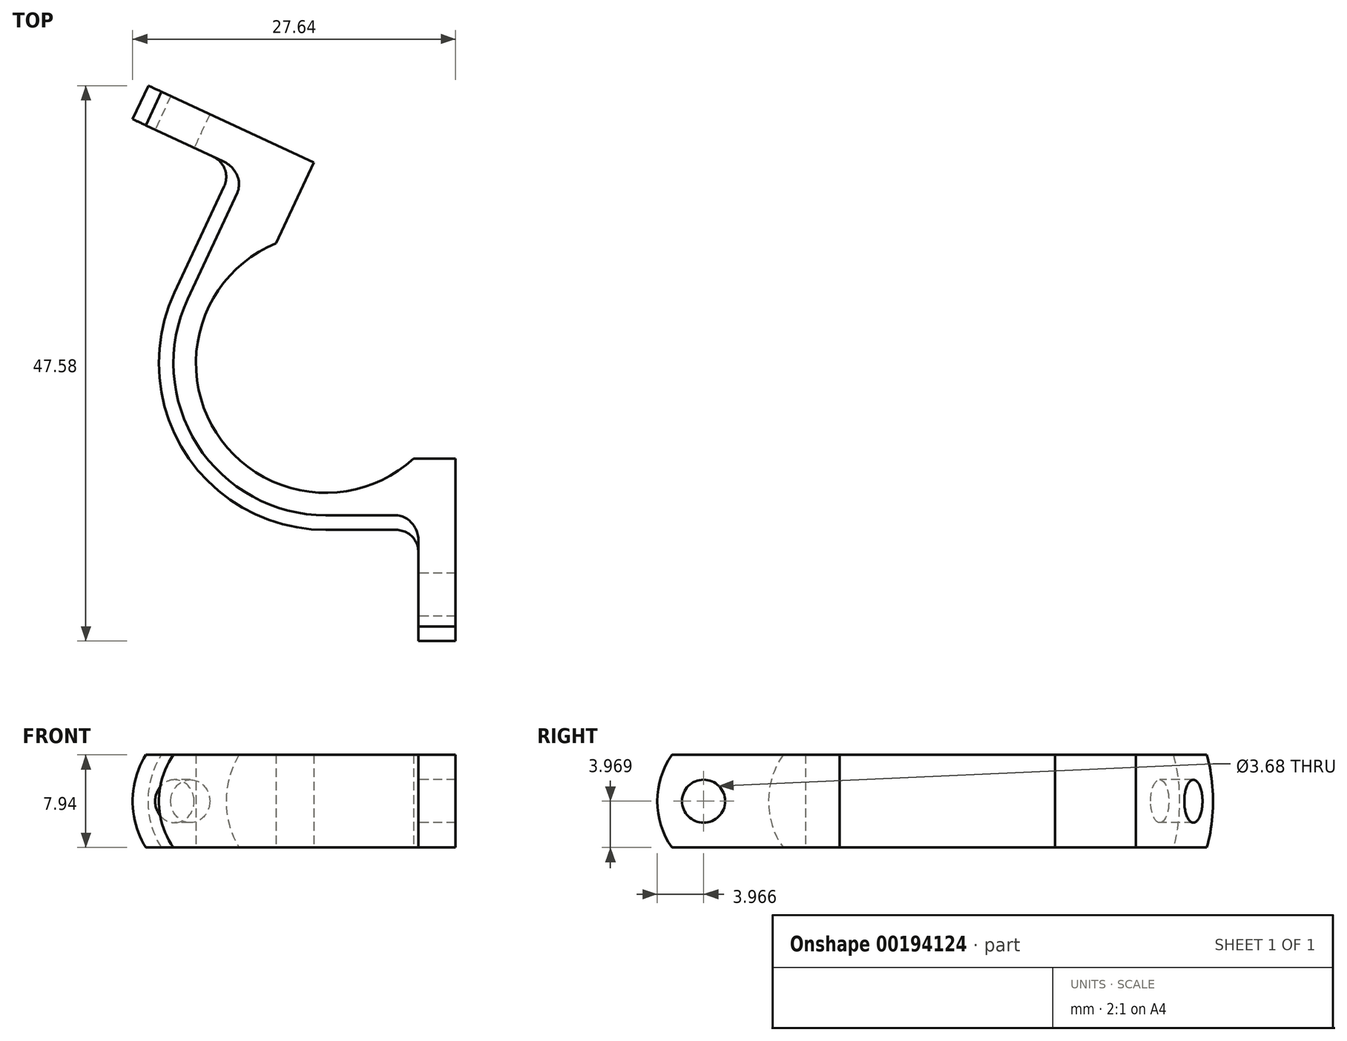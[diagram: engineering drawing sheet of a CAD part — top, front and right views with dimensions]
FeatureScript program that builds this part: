
annotation { "Feature Type Name" : "Feature", "Feature Type Description" : "" }
export const myFeature = defineFeature(function(context is Context, id is Id, definition is map)
    precondition{}
    {
        {
            var Q0;
            Q0=qCreatedBy(makeId("Top.planeOp"),FACE);
            var sketch = newSketch(context, id + "F0", { "sketchPlane" : qUnion([Q0])});
            skCircle(sketch, "E0", {"center": v(0, 0) * mm, "radius": 11.11 * mm, "construction": true});
            skLineSegment(sketch, "E1", {"start": v(11.11, -44.88) * mm, "end": v(11.11, 11.5) * mm, "construction": true});
            skLineSegment(sketch, "E2", {"start": v(11.11, 11.5) * mm, "end": v(-38.46, 34.63) * mm, "construction": true});
            skLineSegment(sketch, "E3", {"start": v(0, -11.11) * mm, "end": v(11.11, -11.11) * mm, "construction": true});
            skLineSegment(sketch, "E4", {"start": v(-10.07, 4.7) * mm, "end": v(-3.68, 18.4) * mm, "construction": true});
            skSolve(sketch);
        }
        {
            var Q0;
            Q0=qCreatedBy(makeId("Right.planeOp"),FACE);
            var sketch = newSketch(context, id + "F1", { "sketchPlane" : qUnion([Q0])});
            skLineSegment(sketch, "E5", {"start": v(-11.11, 0) * mm, "end": v(-11.11, 7.94) * mm});
            skLineSegment(sketch, "E6", {"start": v(-11.11, 7.94) * mm, "end": v(-13.04, 7.94) * mm});
            skLineSegment(sketch, "E7", {"start": v(-13.04, 0) * mm, "end": v(-11.11, 0) * mm});
            skArc(sketch, "E8", {"start": v(-13.04, 7.94) * mm, "mid": v(-14.29, 3.97) * mm, "end": v(-13.04, 0) * mm});
            skLineSegment(sketch, "E9", {"start": v(-13.04, 0) * mm, "end": v(-15.82, 3.97) * mm, "construction": true});
            skLineSegment(sketch, "E10", {"start": v(-14.29, 3.97) * mm, "end": v(-11.11, 3.97) * mm, "construction": true});
            skLineSegment(sketch, "E11", {"start": v(0, 0) * mm, "end": v(0, 7.94) * mm, "construction": true});
            skSolve(sketch);
        }
        {
            var Q0;
            Q0=makeQuery(id+"F1.imprint","IMPRINT",FACE,{"disambiguationData":[TD([[makeQuery(id+"F1.imprint","IMPRINT",EDGE,{"derivedFrom":sQuery(id+"F1.wireOp",EDGE,"E5")}),1.0]])]});
            var Q1;
            Q1=sQuery(id+"F1.wireOp",EDGE,"E11");
            revolve(context, id + "F2", {"entities" : qUnion([Q0]), "axis" : qUnion([Q1]), "revolveType" : RevolveType.FULL});
        }
        {
            var Q0;
            Q0=makeQuery(id+"F2.opRevolve","SWEPT_FACE",FACE,{"disambiguationData":[OSD([sQuery(id+"F1.wireOp",EDGE,"E6")])]});
            var sketch = newSketch(context, id + "F3", { "sketchPlane" : qUnion([Q0])});
            skArc(sketch, "E12", {"start": v(0, -11.11) * mm, "mid": v(9.37, 5.97) * mm, "end": v(-10.07, 4.7) * mm});
            skArc(sketch, "E13", {"start": v(0, -14.29) * mm, "mid": v(12.05, 7.68) * mm, "end": v(-12.95, 6.04) * mm});
            skLineSegment(sketch, "E14", {"start": v(0, 0) * mm, "end": v(-10.07, 4.7) * mm, "construction": true});
            skLineSegment(sketch, "E15", {"start": v(-10.07, 4.7) * mm, "end": v(-12.95, 6.04) * mm});
            skLineSegment(sketch, "E16", {"start": v(0, -11.11) * mm, "end": v(0, -14.29) * mm});
            skSolve(sketch);
        }
        {
            var Q0;
            Q0 = qSketchRegion(id + "F3", true);
            var Q1;
            Q1=makeQuery(id+"F2.opRevolve","SWEPT_FACE",FACE,{"disambiguationData":[OSD([sQuery(id+"F1.wireOp",EDGE,"E7")])]});
            extrude(context, id + "F4", {"entities" : qUnion([Q0]), "operationType" : NewBodyOperationType.REMOVE, "endBound" : BoundingType.UP_TO_SURFACE, "oppositeDirection" : true, "endBoundEntityFace" : qUnion([Q1]), "depth" : 25.4 * mm});
        }
        {
            var Q0;
            Q0=makeQuery(id+"F4.boolean.opBoolean","COPY",FACE,{"derivedFrom":makeQuery(id+"F4.opExtrude","SWEPT_FACE",FACE,{"disambiguationData":[OSD([sQuery(id+"F3.wireOp",EDGE,"E16")])]})});
            var Q1;
            Q1=sQuery(id+"F0.wireOp",VERTEX,"E3.end");
            extrude(context, id + "F5", {"entities" : qUnion([Q0]), "operationType" : NewBodyOperationType.ADD, "endBound" : BoundingType.UP_TO_VERTEX, "endBoundEntityVertex" : qUnion([Q1]), "depth" : 25.4 * mm});
        }
        {
            var Q0;
            Q0=makeQuery(id+"F4.boolean.opBoolean","COPY",FACE,{"derivedFrom":makeQuery(id+"F4.opExtrude","SWEPT_FACE",FACE,{"disambiguationData":[OSD([sQuery(id+"F3.wireOp",EDGE,"E15")])]})});
            var Q1;
            Q1=sQuery(id+"F0.wireOp",VERTEX,"E4.end");
            extrude(context, id + "F6", {"entities" : qUnion([Q0]), "operationType" : NewBodyOperationType.ADD, "endBound" : BoundingType.UP_TO_VERTEX, "endBoundEntityVertex" : qUnion([Q1]), "depth" : 25.4 * mm});
        }
        {
            var Q0;
            Q0=qCreatedBy(makeId("Top.planeOp"),FACE);
            var sketch = newSketch(context, id + "F7", { "sketchPlane" : qUnion([Q0])});
            skLineSegment(sketch, "E17", {"start": v(-10.07, 4.7) * mm, "end": v(0, -11.11) * mm, "construction": true});
            skLineSegment(sketch, "E18", {"start": v(0, 0) * mm, "end": v(-5.97, 9.37) * mm, "construction": true});
            skLineSegment(sketch, "E19", {"start": v(0, 0) * mm, "end": v(5.97, -9.37) * mm, "construction": true});
            skLineSegment(sketch, "E20", {"start": v(7.5, -8.2) * mm, "end": v(0, 0) * mm, "construction": true});
            skLineSegment(sketch, "E21", {"start": v(0, 0) * mm, "end": v(-4.25, 10.27) * mm, "construction": true});
            skArc(sketch, "E22", {"start": v(0, -11.11) * mm, "mid": v(4.03, -10.36) * mm, "end": v(7.5, -8.2) * mm});
            skLineSegment(sketch, "E23", {"start": v(7.5, -8.2) * mm, "end": v(11.11, -8.2) * mm});
            skLineSegment(sketch, "E24", {"start": v(11.11, -8.2) * mm, "end": v(11.11, -11.11) * mm});
            skLineSegment(sketch, "E25", {"start": v(11.11, -11.11) * mm, "end": v(0, -11.11) * mm});
            skArc(sketch, "E26", {"start": v(-4.25, 10.27) * mm, "mid": v(-7.68, 8.03) * mm, "end": v(-10.07, 4.7) * mm});
            skLineSegment(sketch, "E27", {"start": v(-10.07, 4.7) * mm, "end": v(-3.68, 18.4) * mm});
            skLineSegment(sketch, "E28", {"start": v(-3.68, 18.4) * mm, "end": v(-1.03, 17.17) * mm});
            skLineSegment(sketch, "E29", {"start": v(-1.03, 17.17) * mm, "end": v(-4.25, 10.27) * mm});
            skLineSegment(sketch, "E30", {"start": v(11.11, -13.04) * mm, "end": v(11.11, -23.81) * mm});
            skLineSegment(sketch, "E31", {"start": v(11.11, -23.81) * mm, "end": v(7.94, -23.81) * mm});
            skLineSegment(sketch, "E32", {"start": v(7.94, -23.81) * mm, "end": v(7.94, -13.04) * mm});
            skLineSegment(sketch, "E33", {"start": v(7.94, -13.04) * mm, "end": v(11.11, -13.04) * mm});
            skLineSegment(sketch, "E34", {"start": v(0, -14.29) * mm, "end": v(11.11, -14.29) * mm, "construction": true});
            skLineSegment(sketch, "E35", {"start": v(11.11, -14.29) * mm, "end": v(11.11, -11.11) * mm, "construction": true});
            skLineSegment(sketch, "E36", {"start": v(-12.95, 6.04) * mm, "end": v(-6.56, 19.75) * mm, "construction": true});
            skLineSegment(sketch, "E37", {"start": v(-6.56, 19.75) * mm, "end": v(-3.68, 18.4) * mm, "construction": true});
            skLineSegment(sketch, "E38", {"start": v(-5.42, 19.22) * mm, "end": v(-15.19, 23.77) * mm});
            skLineSegment(sketch, "E39", {"start": v(-15.19, 23.77) * mm, "end": v(-16.53, 20.9) * mm});
            skLineSegment(sketch, "E40", {"start": v(-16.53, 20.9) * mm, "end": v(-6.76, 16.34) * mm});
            skLineSegment(sketch, "E41", {"start": v(-6.76, 16.34) * mm, "end": v(-5.42, 19.22) * mm});
            skSolve(sketch);
        }
        {
            var Q0;
            Q0 = qSketchRegion(id + "F7", true);
            var Q1;
            {var subQ0=sQuery(id+"F3.wireOp",EDGE,"E15");var subQ1=sQuery(id+"F3.wireOp",EDGE,"E16");Q1=makeQuery(id+"F6.boolean.opBoolean","MERGE",FACE,{"derivedFrom":[makeQuery(id+"F5.boolean.opBoolean","MERGE",FACE,{"derivedFrom":[makeQuery(id+"F2.opRevolve","SWEPT_FACE",FACE,{"disambiguationData":[OSD([sQuery(id+"F1.wireOp",EDGE,"E6")])]}),makeQuery(id+"F5.opExtrude","SWEPT_FACE",FACE,{"disambiguationData":[OSD([subQ1]),TDD([makeQuery(id+"F4.boolean.opBoolean","COPY",EDGE,{"derivedFrom":makeQuery(id+"F4.opExtrude","CAP_EDGE",EDGE,{"disambiguationData":[OSD([subQ1])],"isStart":true})})])]})]}),makeQuery(id+"F6.opExtrude","SWEPT_FACE",FACE,{"disambiguationData":[OSD([subQ0]),TDD([makeQuery(id+"F4.boolean.opBoolean","COPY",EDGE,{"derivedFrom":makeQuery(id+"F4.opExtrude","CAP_EDGE",EDGE,{"disambiguationData":[OSD([subQ0])],"isStart":true})})])]})]});}
            extrude(context, id + "F8", {"entities" : qUnion([Q0]), "operationType" : NewBodyOperationType.ADD, "endBound" : BoundingType.UP_TO_SURFACE, "endBoundEntityFace" : qUnion([Q1]), "depth" : 25.4 * mm});
        }
        {
            var Q0;
            Q0=makeQuery(id+"F8.opExtrude","SWEPT_FACE",FACE,{"disambiguationData":[OSD([sQuery(id+"F7.wireOp",EDGE,"E32")])]});
            var sketch = newSketch(context, id + "F9", { "sketchPlane" : qUnion([Q0])});
            skArc(sketch, "E42", {"start": v(22.56, 0) * mm, "mid": v(23.81, 3.97) * mm, "end": v(22.56, 7.94) * mm});
            skLineSegment(sketch, "E43", {"start": v(22.56, 7.94) * mm, "end": v(23.81, 7.94) * mm});
            skLineSegment(sketch, "E44", {"start": v(23.81, 7.94) * mm, "end": v(23.81, 0) * mm});
            skLineSegment(sketch, "E45", {"start": v(23.81, 0) * mm, "end": v(22.56, 0) * mm});
            skCircle(sketch, "E46", {"center": v(19.84, 3.97) * mm, "radius": 3.97 * mm, "construction": true});
            skCircle(sketch, "E47", {"center": v(19.84, 3.97) * mm, "radius": 1.84 * mm});
            skSolve(sketch);
        }
        {
            var Q0;
            Q0=makeQuery(id+"F9.imprint","IMPRINT",FACE,{"disambiguationData":[TD([[makeQuery(id+"F9.imprint","IMPRINT",EDGE,{"derivedFrom":sQuery(id+"F9.wireOp",EDGE,"E47")}),1.0]])]});
            var Q1;
            {var subQ0=sQuery(id+"F9.wireOp",EDGE,"E43");Q1=makeQuery(id+"F9.imprint","IMPRINT",FACE,{"disambiguationData":[TD([[makeQuery(id+"F9.imprint","IMPRINT",EDGE,{"derivedFrom":subQ0}),-1.0]])]});}
            var Q2;
            {var subQ0=sQuery(id+"F9.wireOp",EDGE,"E45");Q2=makeQuery(id+"F9.imprint","IMPRINT",FACE,{"disambiguationData":[TD([[makeQuery(id+"F9.imprint","IMPRINT",EDGE,{"derivedFrom":subQ0}),-1.0]])]});}
            extrude(context, id + "F10", {"entities" : qUnion([Q0, Q1, Q2]), "operationType" : NewBodyOperationType.REMOVE, "endBound" : BoundingType.UP_TO_NEXT, "oppositeDirection" : true, "depth" : 25.4 * mm});
        }
        {
            var Q0;
            Q0=makeQuery(id+"F8.opExtrude","SWEPT_FACE",FACE,{"disambiguationData":[OSD([sQuery(id+"F7.wireOp",EDGE,"E40")])]});
            var sketch = newSketch(context, id + "F11", { "sketchPlane" : qUnion([Q0])});
            skArc(sketch, "E48", {"start": v(-22.56, 7.94) * mm, "mid": v(-23.81, 3.97) * mm, "end": v(-22.56, 0) * mm});
            skLineSegment(sketch, "E49", {"start": v(-22.56, 7.94) * mm, "end": v(-23.81, 7.94) * mm});
            skLineSegment(sketch, "E50", {"start": v(-23.81, 7.94) * mm, "end": v(-23.81, 0) * mm});
            skLineSegment(sketch, "E51", {"start": v(-23.81, 0) * mm, "end": v(-22.56, 0) * mm});
            skCircle(sketch, "E52", {"center": v(-19.84, 3.97) * mm, "radius": 3.97 * mm, "construction": true});
            skCircle(sketch, "E53", {"center": v(-19.84, 3.97) * mm, "radius": 1.84 * mm});
            skSolve(sketch);
        }
        {
            var Q0;
            Q0=makeQuery(id+"F11.imprint","IMPRINT",FACE,{"disambiguationData":[TD([[makeQuery(id+"F11.imprint","IMPRINT",EDGE,{"derivedFrom":sQuery(id+"F11.wireOp",EDGE,"E53")}),1.0]])]});
            var Q1;
            {var subQ0=sQuery(id+"F11.wireOp",EDGE,"E49");Q1=makeQuery(id+"F11.imprint","IMPRINT",FACE,{"disambiguationData":[TD([[makeQuery(id+"F11.imprint","IMPRINT",EDGE,{"derivedFrom":subQ0}),1.0]])]});}
            var Q2;
            {var subQ0=sQuery(id+"F11.wireOp",EDGE,"E51");Q2=makeQuery(id+"F11.imprint","IMPRINT",FACE,{"disambiguationData":[TD([[makeQuery(id+"F11.imprint","IMPRINT",EDGE,{"derivedFrom":subQ0}),1.0]])]});}
            extrude(context, id + "F12", {"entities" : qUnion([Q0, Q1, Q2]), "operationType" : NewBodyOperationType.REMOVE, "endBound" : BoundingType.UP_TO_NEXT, "oppositeDirection" : true, "depth" : 25.4 * mm});
        }
        {
            var Q0;
            Q0=makeQuery(id+"F8.boolean.opBoolean","INTERSECT",EDGE,{"derivedFrom":[makeQuery(id+"F6.opExtrude","SWEPT_FACE",FACE,{"disambiguationData":[OSD([sQuery(id+"F1.wireOp",EDGE,"E8"),sQuery(id+"F3.wireOp",EDGE,"E15")])]}),makeQuery(id+"F8.opExtrude","SWEPT_FACE",FACE,{"disambiguationData":[OSD([sQuery(id+"F7.wireOp",EDGE,"E40")])]})]});
            var Q1;
            Q1=makeQuery(id+"F8.boolean.opBoolean","INTERSECT",EDGE,{"derivedFrom":[makeQuery(id+"F5.opExtrude","SWEPT_FACE",FACE,{"disambiguationData":[OSD([sQuery(id+"F1.wireOp",EDGE,"E8"),sQuery(id+"F3.wireOp",EDGE,"E16")])]}),makeQuery(id+"F8.opExtrude","SWEPT_FACE",FACE,{"disambiguationData":[OSD([sQuery(id+"F7.wireOp",EDGE,"E32")])]})]});
            fillet(context, id + "F13", {"entities" : qUnion([Q0, Q1]), "radius" : 1.9 * mm, "tangentPropagation" : true, "allowEdgeOverflow" : false});
        }
    });
